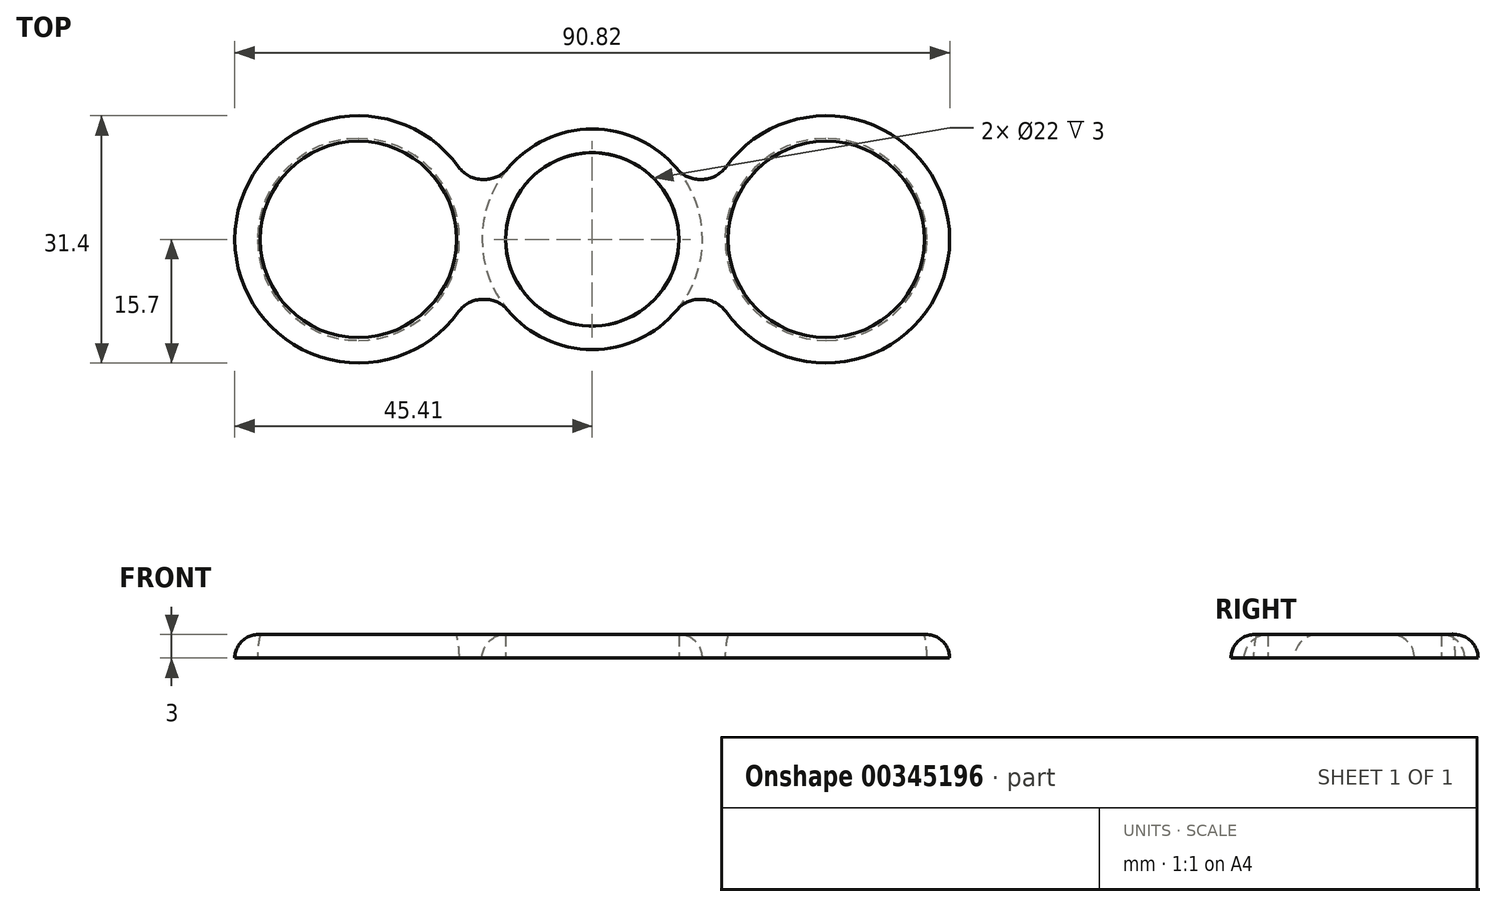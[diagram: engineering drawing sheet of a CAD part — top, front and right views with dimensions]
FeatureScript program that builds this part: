
annotation { "Feature Type Name" : "Feature", "Feature Type Description" : "" }
export const myFeature = defineFeature(function(context is Context, id is Id, definition is map)
    precondition{}
    {
        {
            var Q0;
            Q0=qCreatedBy(makeId("Top.planeOp"),FACE);
            var sketch = newSketch(context, id + "F0", { "sketchPlane" : qUnion([Q0])});
            skCircle(sketch, "E0", {"center": v(0, 0) * mm, "radius": 11 * mm});
            skArc(sketch, "E1", {"start": v(10.74, 8.98) * mm, "mid": v(-14, 0) * mm, "end": v(10.74, -8.98) * mm});
            skCircle(sketch, "E2", {"center": v(29.7, 0) * mm, "radius": 10.16 * mm});
            skArc(sketch, "E3", {"start": v(16.98, -9.2) * mm, "mid": v(45.4, 0) * mm, "end": v(16.98, 9.2) * mm});
            skLineSegment(sketch, "E4", {"start": v(13.66, 7.62) * mm, "end": v(13.9, 7.62) * mm});
            skLineSegment(sketch, "E5", {"start": v(13.66, -7.62) * mm, "end": v(13.9, -7.62) * mm});
            skPoint(sketch, "E6.visualSharp", {"position": v(11.74, 7.62) * mm});
            skArc(sketch, "E6.filletArc", {"start": v(10.74, 8.98) * mm, "mid": v(12.05, 7.98) * mm, "end": v(13.66, 7.62) * mm});
            skPoint(sketch, "E7.visualSharp", {"position": v(15.98, 7.62) * mm});
            skArc(sketch, "E7.filletArc", {"start": v(13.9, 7.62) * mm, "mid": v(15.63, 8.04) * mm, "end": v(16.98, 9.2) * mm});
            skPoint(sketch, "E8.visualSharp", {"position": v(11.74, -7.62) * mm});
            skArc(sketch, "E8.filletArc", {"start": v(13.66, -7.62) * mm, "mid": v(12.05, -7.98) * mm, "end": v(10.74, -8.98) * mm});
            skPoint(sketch, "E9.visualSharp", {"position": v(15.98, -7.62) * mm});
            skArc(sketch, "E9.filletArc", {"start": v(16.98, -9.2) * mm, "mid": v(15.63, -8.04) * mm, "end": v(13.9, -7.62) * mm});
            skSolve(sketch);
        }
        {
            var Q0;
            Q0=makeQuery(id+"F0.imprint","IMPRINT",FACE,{"disambiguationData":[TD([[makeQuery(id+"F0.imprint","IMPRINT",EDGE,{"derivedFrom":sQuery(id+"F0.wireOp",EDGE,"E2")}),-1.0]])]});
            var Q1;
            Q1=makeQuery(id+"F0.imprint","IMPRINT",FACE,{"disambiguationData":[TD([[makeQuery(id+"F0.imprint","IMPRINT",EDGE,{"derivedFrom":sQuery(id+"F0.wireOp",EDGE,"E0")}),-1.0]])]});
            extrude(context, id + "F1", {"entities" : qUnion([Q0, Q1]), "depth" : 3 * mm});
        }
        {
            var Q0;
            Q0=qCreatedBy(makeId("Top.planeOp"),FACE);
            var sketch = newSketch(context, id + "F2", { "sketchPlane" : qUnion([Q0])});
            skArc(sketch, "E10", {"start": v(29.7, 12.83) * mm, "mid": v(16.88, 0) * mm, "end": v(29.7, -12.83) * mm});
            skLineSegment(sketch, "E11", {"start": v(29.7, 12.83) * mm, "end": v(29.7, -12.83) * mm});
            skSolve(sketch);
        }
        {
            var Q0;
            Q0 = qSketchRegion(id + "F2", true);
            var Q1;
            Q1=sQuery(id+"F2.wireOp",EDGE,"E11");
            revolve(context, id + "F3", {"operationType" : NewBodyOperationType.REMOVE, "entities" : qUnion([Q0]), "axis" : qUnion([Q1]), "revolveType" : RevolveType.FULL, "oppositeDirection" : true});
        }
        {
            var Q0;
            Q0=makeQuery(id+"F1.opExtrude","CAP_EDGE",EDGE,{"disambiguationData":[OSD([sQuery(id+"F0.wireOp",EDGE,"E1")])],"isStart":false});
            fillet(context, id + "F4", {"entities" : qUnion([Q0]), "radius" : 3 * mm, "tangentPropagation" : true, "allowEdgeOverflow" : false});
        }
        {
            var Q0;
            Q0=makeQuery(id+"F1.opExtrude","SWEPT_BODY",BODY,{"disambiguationData":[OSD([sQuery(id+"F0.wireOp",EDGE,"E0"),sQuery(id+"F0.wireOp",EDGE,"E1"),sQuery(id+"F0.wireOp",EDGE,"E2"),sQuery(id+"F0.wireOp",EDGE,"E3"),sQuery(id+"F0.wireOp",EDGE,"E4"),sQuery(id+"F0.wireOp",EDGE,"E5"),sQuery(id+"F0.wireOp",EDGE,"E6.filletArc"),sQuery(id+"F0.wireOp",EDGE,"E7.filletArc"),sQuery(id+"F0.wireOp",EDGE,"E8.filletArc"),sQuery(id+"F0.wireOp",EDGE,"E9.filletArc")])]});
            var Q1;
            Q1=makeQuery(id+"F4.opFillet","BLEND_FACE",FACE,{"disambiguationData":[OSD([sQuery(id+"F0.wireOp",EDGE,"E1")])]});
            circularPattern(context, id + "F5", {"entities" : qUnion([Q0]), "axis" : qUnion([Q1]), "angle" : 360 * degree, "instanceCount" : 2, "equalSpace" : true});
        }
    });
